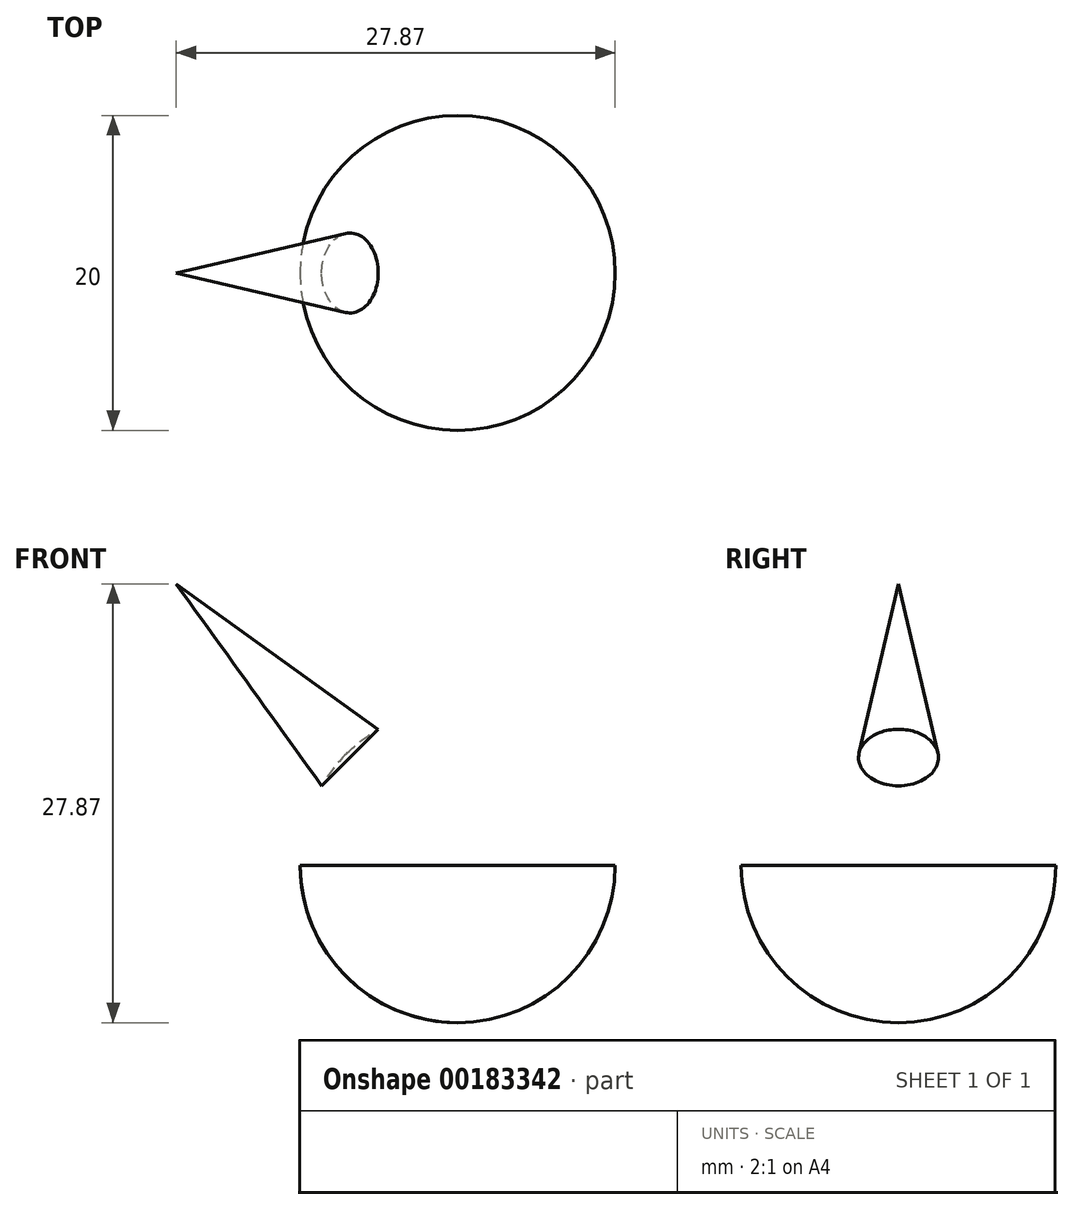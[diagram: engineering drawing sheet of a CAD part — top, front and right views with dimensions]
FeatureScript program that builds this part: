
annotation { "Feature Type Name" : "Feature", "Feature Type Description" : "" }
export const myFeature = defineFeature(function(context is Context, id is Id, definition is map)
    precondition{}
    {
        {
            var Q0;
            Q0=qCreatedBy(makeId("Front.planeOp"),FACE);
            var sketch = newSketch(context, id + "F0", { "sketchPlane" : qUnion([Q0])});
            skCircle(sketch, "E0", {"center": v(0, 0) * mm, "radius": 10 * mm});
            skLineSegment(sketch, "E1", {"start": v(0, 0) * mm, "end": v(-10, 0) * mm});
            skLineSegment(sketch, "E2", {"start": v(0, 0) * mm, "end": v(0, 10) * mm});
            skLineSegment(sketch, "E3", {"start": v(0, 10) * mm, "end": v(0, -10) * mm});
            skLineSegment(sketch, "E4", {"start": v(-5, 0) * mm, "end": v(0, 5) * mm});
            skLineSegment(sketch, "E5", {"start": v(0, 0) * mm, "end": v(-17.87, 17.87) * mm});
            skLineSegment(sketch, "E6", {"start": v(0, 5) * mm, "end": v(-17.87, 17.87) * mm});
            skLineSegment(sketch, "E7", {"start": v(-5, 0) * mm, "end": v(-17.87, 17.87) * mm});
            skSolve(sketch);
        }
        {
            var Q0;
            {var subQ0=sQuery(id+"F0.wireOp",EDGE,"E3");var subQ1=sQuery(id+"F0.wireOp",EDGE,"E0");var subQ2=makeQuery(id+"F0.imprint","INTERSECT",VERTEX,{"disambiguationData":[OD(0.0)],"derivedFrom":[subQ1,subQ0]});Q0=makeQuery(id+"F0.imprint","IMPRINT",FACE,{"disambiguationData":[TD([[makeQuery(id+"F0.imprint","IMPRINT",EDGE,{"disambiguationData":[TD([[subQ2,1.0]])],"derivedFrom":subQ1}),1.0]])]});}
            var Q1;
            Q1=sQuery(id+"F0.wireOp",EDGE,"E3");
            revolve(context, id + "F1", {"entities" : qUnion([Q0]), "axis" : qUnion([Q1]), "revolveType" : RevolveType.FULL});
        }
        {
            var Q0;
            {var subQ0=sQuery(id+"F0.wireOp",EDGE,"E6");var subQ1=sQuery(id+"F0.wireOp",EDGE,"E0");var subQ2=makeQuery(id+"F0.imprint","INTERSECT",VERTEX,{"derivedFrom":[subQ1,subQ0]});Q0=makeQuery(id+"F0.imprint","IMPRINT",FACE,{"disambiguationData":[TD([[makeQuery(id+"F0.imprint","IMPRINT",EDGE,{"disambiguationData":[TD([[subQ2,-1.0]])],"derivedFrom":subQ1}),-1.0]])]});}
            var Q1;
            Q1=sQuery(id+"F0.wireOp",EDGE,"E5");
            revolve(context, id + "F2", {"operationType" : NewBodyOperationType.ADD, "entities" : qUnion([Q0]), "axis" : qUnion([Q1]), "revolveType" : RevolveType.FULL});
        }
    });
